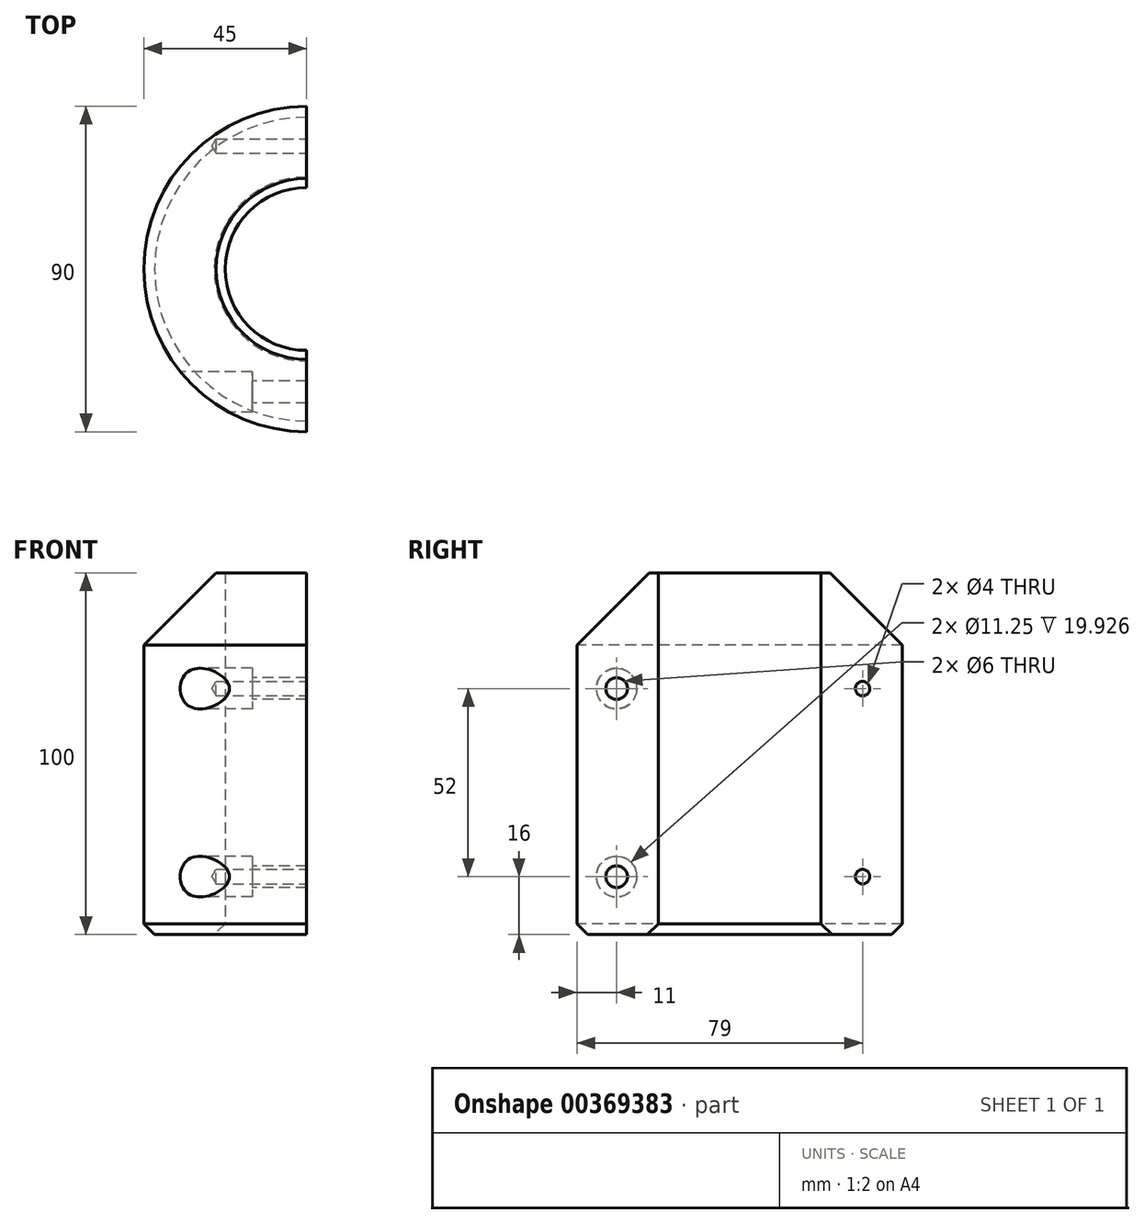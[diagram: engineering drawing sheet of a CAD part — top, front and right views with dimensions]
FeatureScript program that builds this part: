
annotation { "Feature Type Name" : "Feature", "Feature Type Description" : "" }
export const myFeature = defineFeature(function(context is Context, id is Id, definition is map)
    precondition{}
    {
        {
            var Q0;
            Q0=qCreatedBy(makeId("Top.planeOp"),FACE);
            var sketch = newSketch(context, id + "F0", { "sketchPlane" : qUnion([Q0])});
            skCircle(sketch, "E0", {"center": v(0, 0) * mm, "radius": 45 * mm});
            skCircle(sketch, "E1", {"center": v(0, 0) * mm, "radius": 22.5 * mm});
            skSolve(sketch);
        }
        {
            var Q0;
            Q0 = qSketchRegion(id + "F0", true);
            extrude(context, id + "F1", {"entities" : qUnion([Q0]), "depth" : 100 * mm});
        }
        {
            var Q0;
            Q0=makeQuery(id+"F1.opExtrude","CAP_EDGE",EDGE,{"disambiguationData":[OSD([sQuery(id+"F0.wireOp",EDGE,"E0")])],"isStart":false});
            chamfer(context, id + "F2", {"entities" : qUnion([Q0]), "width" : 20 * mm, "tangentPropagation" : true});
        }
        {
            var Q0;
            Q0=makeQuery(id+"F1.opExtrude","CAP_EDGE",EDGE,{"disambiguationData":[OSD([sQuery(id+"F0.wireOp",EDGE,"E0")])],"isStart":true});
            var Q1;
            Q1=makeQuery(id+"F1.opExtrude","CAP_FACE",FACE,{"disambiguationData":[OSD([sQuery(id+"F0.wireOp",EDGE,"E0"),sQuery(id+"F0.wireOp",EDGE,"E1")])],"isStart":true});
            chamfer(context, id + "F3", {"entities" : qUnion([Q0, Q1]), "width" : 3 * mm, "tangentPropagation" : true});
        }
        {
            var Q0;
            Q0=qCreatedBy(makeId("Top.planeOp"),FACE);
            var sketch = newSketch(context, id + "F4", { "sketchPlane" : qUnion([Q0])});
            skLineSegment(sketch, "E2.bottom", {"start": v(0, 68.55) * mm, "end": v(48.85, 68.55) * mm});
            skLineSegment(sketch, "E2.top", {"start": v(0, -64.06) * mm, "end": v(48.85, -64.06) * mm});
            skLineSegment(sketch, "E2.left", {"start": v(0, 68.55) * mm, "end": v(0, -64.06) * mm});
            skLineSegment(sketch, "E2.right", {"start": v(48.85, 68.55) * mm, "end": v(48.85, -64.06) * mm});
            skSolve(sketch);
        }
        {
            var Q0;
            Q0 = qSketchRegion(id + "F4", true);
            extrude(context, id + "F5", {"entities" : qUnion([Q0]), "operationType" : NewBodyOperationType.REMOVE, "depth" : 100 * mm});
        }
        {
            var Q0;
            Q0=makeQuery(id+"F5.boolean.opBoolean","COPY",FACE,{"disambiguationData":[OD(0.0)],"derivedFrom":makeQuery(id+"F5.opExtrude","SWEPT_FACE",FACE,{"disambiguationData":[OSD([sQuery(id+"F4.wireOp",EDGE,"E2.left")])]})});
            cPlane(context, id + "F6", {"entities" : qUnion([Q0]), "cplaneType" : CPlaneType.OFFSET, "offset" : 50 * mm, "oppositeDirection" : true, "width" : 150 * mm, "height" : 150 * mm});
        }
        {
            var Q0;
            Q0=makeQuery(id+"F5.boolean.opBoolean","COPY",FACE,{"disambiguationData":[OD(0.0)],"derivedFrom":makeQuery(id+"F5.opExtrude","SWEPT_FACE",FACE,{"disambiguationData":[OSD([sQuery(id+"F4.wireOp",EDGE,"E2.left")])]})});
            var sketch = newSketch(context, id + "F7", { "sketchPlane" : qUnion([Q0])});
            skPoint(sketch, "E3", {"position": v(-34, 16) * mm});
            skPoint(sketch, "E4", {"position": v(-34, 68) * mm});
            skPoint(sketch, "E5.MirrorP", {"position": v(34, 16) * mm});
            skPoint(sketch, "E6.MirrorP", {"position": v(34, 68) * mm});
            skSolve(sketch);
        }
        {
            var Q0;
            Q0=sQuery(id+"F7.wireOp",VERTEX,"E6.MirrorP");
            var Q1;
            Q1=sQuery(id+"F7.wireOp",VERTEX,"E5.MirrorP");
            var Q2;
            Q2=makeQuery(id+"F1.opExtrude","SWEPT_BODY",BODY,{"disambiguationData":[OSD([sQuery(id+"F0.wireOp",EDGE,"E0"),sQuery(id+"F0.wireOp",EDGE,"E1")])]});
            hole(context, id + "F8", {"style" : HoleStyle.SIMPLE, "endStyle" : HoleEndStyle.BLIND, "standardTappedOrClearance" : lookupTablePath({ "standard" : "ISO", "size" : "4", "type" : "Drilled" }), "standardBlindInLast" : lookupTablePath({ "standard" : "ISO", "size" : "4", "type" : "Drilled" }), "holeDiameter" : 4 * mm, "holeDepth" : 25 * mm, "isTappedThrough" : true, "tappedDepth" : 12 * mm, "tapClearance" : 3, "startFromSketch" : true, "locations" : qUnion([Q0, Q1]), "scope" : qUnion([Q2])});
        }
        {
            var Q0;
            Q0=qCreatedBy(id+"F6.planeOp",FACE);
            var sketch = newSketch(context, id + "F9", { "sketchPlane" : qUnion([Q0])});
            skPoint(sketch, "E7", {"position": v(-34, 68) * mm});
            skPoint(sketch, "E8", {"position": v(-34, 16) * mm});
            skSolve(sketch);
        }
        {
            var Q0;
            Q0=sQuery(id+"F9.wireOp",VERTEX,"E7");
            var Q1;
            Q1=sQuery(id+"F9.wireOp",VERTEX,"E8");
            var Q2;
            Q2=makeQuery(id+"F1.opExtrude","SWEPT_BODY",BODY,{"disambiguationData":[OSD([sQuery(id+"F0.wireOp",EDGE,"E0"),sQuery(id+"F0.wireOp",EDGE,"E1")])]});
            hole(context, id + "F10", {"style" : HoleStyle.C_BORE, "endStyle" : HoleEndStyle.THROUGH, "oppositeDirection" : true, "standardTappedOrClearance" : lookupTablePath({ "standard" : "ISO", "size" : "6", "type" : "Drilled" }), "standardBlindInLast" : lookupTablePath({ "standard" : "ISO", "size" : "6", "type" : "Drilled" }), "holeDiameter" : 6 * mm, "cBoreDiameter" : 11.25 * mm, "cBoreDepth" : 35 * mm, "isTappedThrough" : true, "tappedDepth" : 12 * mm, "tapClearance" : 3, "startFromSketch" : true, "locations" : qUnion([Q0, Q1]), "scope" : qUnion([Q2])});
        }
    });
